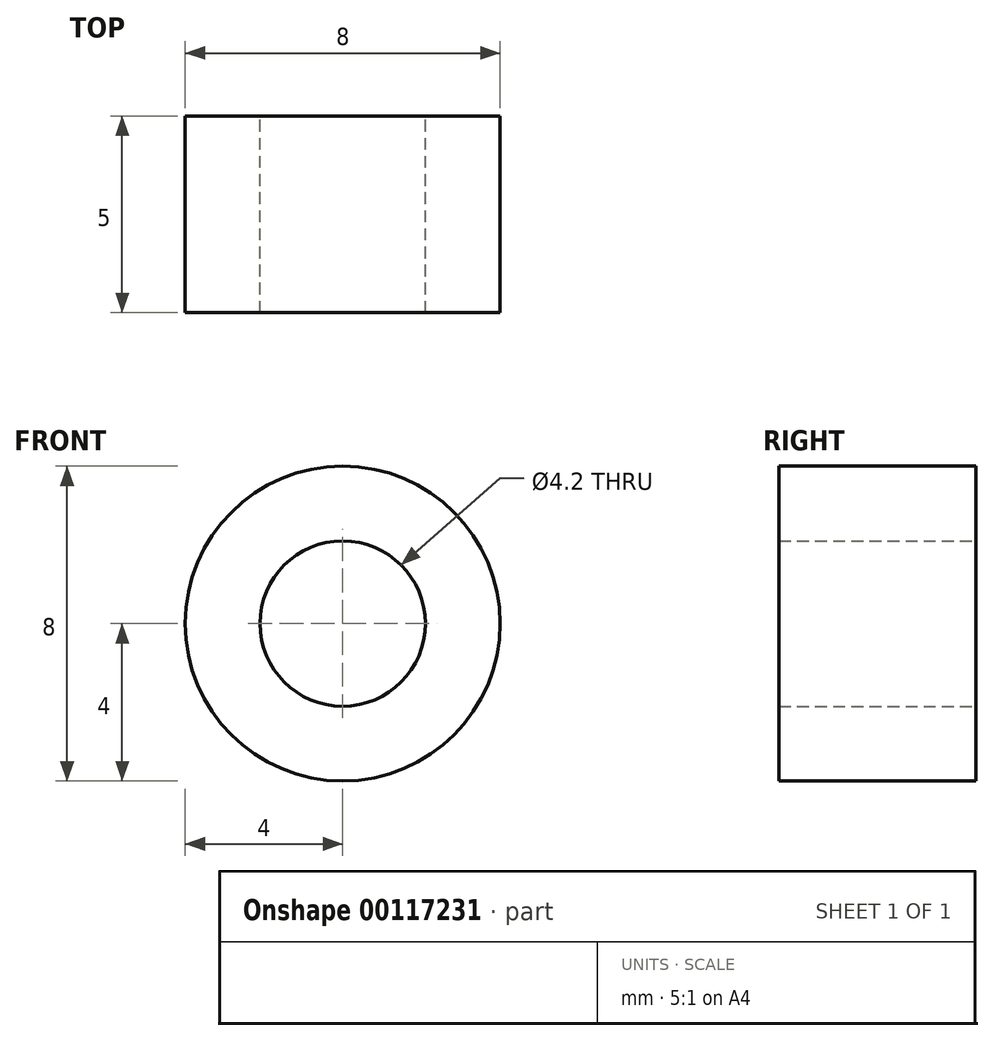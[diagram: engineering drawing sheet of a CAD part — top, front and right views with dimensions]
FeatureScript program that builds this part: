
annotation { "Feature Type Name" : "Feature", "Feature Type Description" : "" }
export const myFeature = defineFeature(function(context is Context, id is Id, definition is map)
    precondition{}
    {
        {
            var Q0;
            Q0=qCreatedBy(makeId("Front.planeOp"),FACE);
            var sketch = newSketch(context, id + "F0", { "sketchPlane" : qUnion([Q0])});
            skCircle(sketch, "E0", {"center": v(0, 0) * mm, "radius": 2.1 * mm});
            skCircle(sketch, "E1", {"center": v(0, 0) * mm, "radius": 4 * mm});
            skSolve(sketch);
        }
        {
            var Q0;
            Q0=makeQuery(id+"F0.imprint","IMPRINT",FACE,{"disambiguationData":[TD([[makeQuery(id+"F0.imprint","IMPRINT",EDGE,{"derivedFrom":sQuery(id+"F0.wireOp",EDGE,"E0")}),-1.0]])]});
            extrude(context, id + "F1", {"entities" : qUnion([Q0]), "depth" : 5 * mm});
        }
    });
